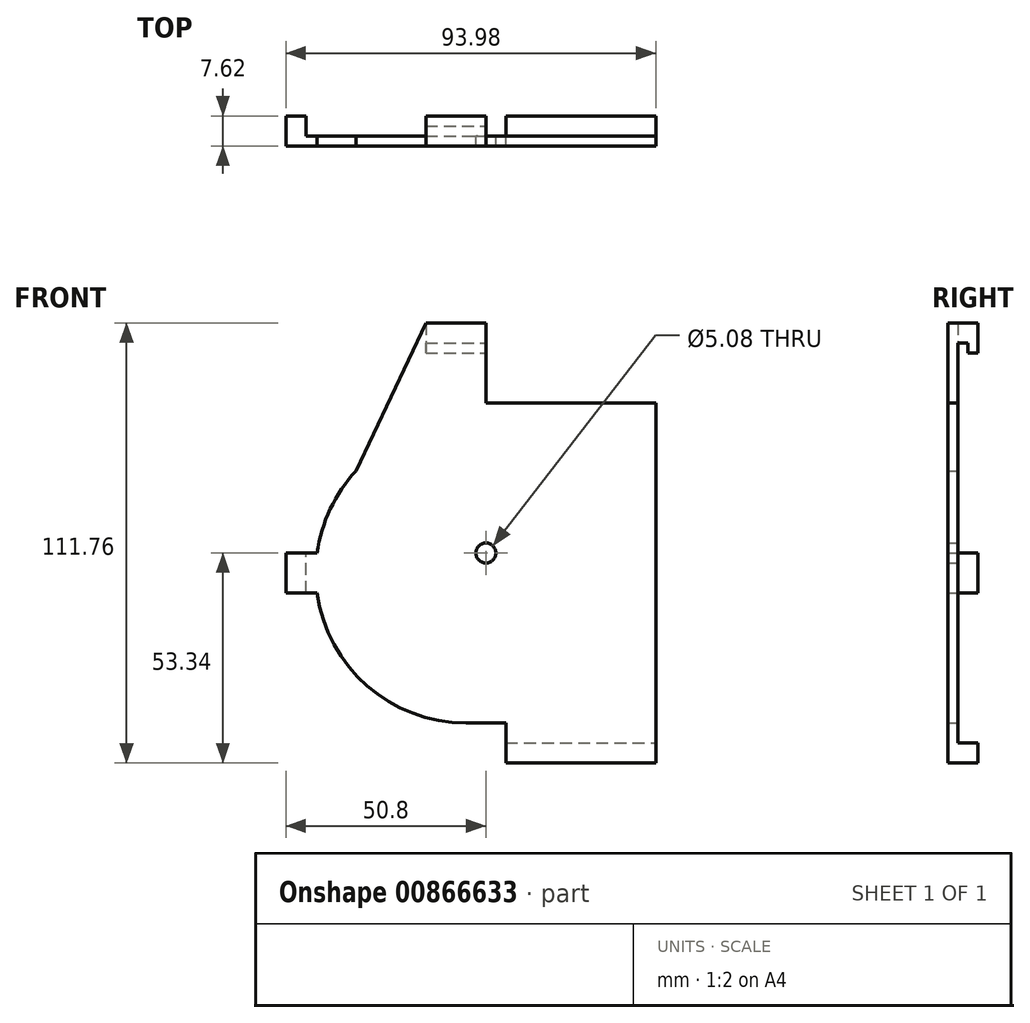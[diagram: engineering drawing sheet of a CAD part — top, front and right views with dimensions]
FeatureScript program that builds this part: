
annotation { "Feature Type Name" : "Feature", "Feature Type Description" : "" }
export const myFeature = defineFeature(function(context is Context, id is Id, definition is map)
    precondition{}
    {
        {
            var Q0;
            Q0=qCreatedBy(makeId("Front.planeOp"),FACE);
            var sketch = newSketch(context, id + "F0", { "sketchPlane" : qUnion([Q0])});
            skLineSegment(sketch, "E0.left", {"start": v(43.18, 43.18) * mm, "end": v(43.18, -38.1) * mm});
            skArc(sketch, "E1", {"start": v(-42.84, -5.08) * mm, "mid": v(-30.16, -28.68) * mm, "end": v(-5.08, -38.1) * mm});
            skLineSegment(sketch, "E2.top", {"start": v(-15.24, 63.5) * mm, "end": v(0, 63.5) * mm});
            skLineSegment(sketch, "E3.top", {"start": v(43.18, 43.18) * mm, "end": v(0, 43.18) * mm});
            skLineSegment(sketch, "E3.right", {"start": v(0, 63.5) * mm, "end": v(0, 43.18) * mm});
            skLineSegment(sketch, "E4.bottom", {"start": v(-50.8, 5.08) * mm, "end": v(-42.84, 5.08) * mm});
            skLineSegment(sketch, "E4.top", {"start": v(-50.8, -5.08) * mm, "end": v(-42.84, -5.08) * mm});
            skLineSegment(sketch, "E4.left", {"start": v(-50.8, 5.08) * mm, "end": v(-50.8, -5.08) * mm});
            skPoint(sketch, "E5.orphan", {"position": v(-43.18, 0) * mm});
            skLineSegment(sketch, "E6", {"start": v(-5.08, -38.1) * mm, "end": v(5.08, -38.1) * mm});
            skLineSegment(sketch, "E7.top", {"start": v(43.18, -48.26) * mm, "end": v(5.08, -48.26) * mm});
            skLineSegment(sketch, "E7.left", {"start": v(43.18, -38.1) * mm, "end": v(43.18, -48.26) * mm});
            skLineSegment(sketch, "E7.right", {"start": v(5.08, -38.1) * mm, "end": v(5.08, -48.26) * mm});
            skArc(sketch, "E8", {"start": v(-32.98, 25.94) * mm, "mid": v(-39.53, 16.28) * mm, "end": v(-42.84, 5.08) * mm});
            skLineSegment(sketch, "E9", {"start": v(0, 63.5) * mm, "end": v(-15.24, 63.5) * mm});
            skLineSegment(sketch, "E10", {"start": v(-32.98, 25.94) * mm, "end": v(-15.24, 63.5) * mm});
            skSolve(sketch);
        }
        {
            var Q0;
            Q0 = qSketchRegion(id + "F0", true);
            extrude(context, id + "F1", {"entities" : qUnion([Q0]), "depth" : 2.54 * mm, "offsetDistance" : 25.4 * mm});
        }
        {
            var Q0;
            Q0=makeQuery(id+"F1.opExtrude","SWEPT_FACE",FACE,{"disambiguationData":[OSD([sQuery(id+"F0.wireOp",EDGE,"E3.right")])]});
            var sketch = newSketch(context, id + "F2", { "sketchPlane" : qUnion([Q0])});
            skLineSegment(sketch, "E11.bottom", {"start": v(0, 63.5) * mm, "end": v(5.08, 63.5) * mm});
            skLineSegment(sketch, "E11.top", {"start": v(2.54, 55.88) * mm, "end": v(5.08, 55.88) * mm});
            skLineSegment(sketch, "E11.left", {"start": v(0, 63.5) * mm, "end": v(0, 58.42) * mm});
            skLineSegment(sketch, "E11.right", {"start": v(5.08, 63.5) * mm, "end": v(5.08, 55.88) * mm});
            skLineSegment(sketch, "E12.top", {"start": v(0, 58.42) * mm, "end": v(2.54, 58.42) * mm});
            skLineSegment(sketch, "E12.right", {"start": v(2.54, 55.88) * mm, "end": v(2.54, 58.42) * mm});
            skSolve(sketch);
        }
        {
            var Q0;
            Q0=makeQuery(id+"F2.imprint","IMPRINT",FACE,{"disambiguationData":[TD([[makeQuery(id+"F2.imprint","IMPRINT",EDGE,{"derivedFrom":sQuery(id+"F2.wireOp",EDGE,"E11.bottom")}),-1.0]])]});
            extrude(context, id + "F3", {"entities" : qUnion([Q0]), "operationType" : NewBodyOperationType.ADD, "oppositeDirection" : true, "depth" : 15.24 * mm, "offsetDistance" : 25.4 * mm});
        }
        {
            var Q0;
            Q0=makeQuery(id+"F1.opExtrude","SWEPT_FACE",FACE,{"disambiguationData":[OSD([sQuery(id+"F0.wireOp",EDGE,"E4.bottom")])]});
            var sketch = newSketch(context, id + "F4", { "sketchPlane" : qUnion([Q0])});
            skLineSegment(sketch, "E13.bottom", {"start": v(-50.8, -2.54) * mm, "end": v(-45.72, -2.54) * mm});
            skLineSegment(sketch, "E13.top", {"start": v(-50.8, 5.08) * mm, "end": v(-45.72, 5.08) * mm});
            skLineSegment(sketch, "E13.left", {"start": v(-50.8, -2.54) * mm, "end": v(-50.8, 5.08) * mm});
            skLineSegment(sketch, "E13.right", {"start": v(-45.72, -2.54) * mm, "end": v(-45.72, 5.08) * mm});
            skSolve(sketch);
        }
        {
            var Q0;
            {var subQ0=sQuery(id+"F4.wireOp",EDGE,"E13.top");Q0=makeQuery(id+"F4.imprint","IMPRINT",FACE,{"disambiguationData":[TD([[makeQuery(id+"F4.imprint","IMPRINT",EDGE,{"derivedFrom":subQ0}),-1.0]])]});}
            extrude(context, id + "F5", {"entities" : qUnion([Q0]), "operationType" : NewBodyOperationType.ADD, "oppositeDirection" : true, "depth" : 10.16 * mm, "offsetDistance" : 25.4 * mm});
        }
        {
            var Q0;
            Q0=makeQuery(id+"F1.opExtrude","CAP_FACE",FACE,{"disambiguationData":[OSD([sQuery(id+"F0.wireOp",EDGE,"E0.top"),sQuery(id+"F0.wireOp",EDGE,"E0.left"),sQuery(id+"F0.wireOp",EDGE,"E1"),sQuery(id+"F0.wireOp",EDGE,"E2.top"),sQuery(id+"F0.wireOp",EDGE,"E3.top"),sQuery(id+"F0.wireOp",EDGE,"E3.right"),sQuery(id+"F0.wireOp",EDGE,"0rXN8d2l-EEdK-oU76-9m5N-EmU7iEtvsEKj"),sQuery(id+"F0.wireOp",EDGE,"cag3bcGU-nAMg-Rm8s-b5UI-sf5c9dMruiX0"),sQuery(id+"F0.wireOp",EDGE,"E4.bottom"),sQuery(id+"F0.wireOp",EDGE,"E4.top"),sQuery(id+"F0.wireOp",EDGE,"E4.left"),sQuery(id+"F0.wireOp",EDGE,"FOCskiKA-atYN-HFuz-2flS-ZA1Z71375tWF.top"),sQuery(id+"F0.wireOp",EDGE,"FOCskiKA-atYN-HFuz-2flS-ZA1Z71375tWF.left"),sQuery(id+"F0.wireOp",EDGE,"FOCskiKA-atYN-HFuz-2flS-ZA1Z71375tWF.right")])],"isStart":true});
            var sketch = newSketch(context, id + "F6", { "sketchPlane" : qUnion([Q0])});
            skCircle(sketch, "E14", {"center": v(0, 5.08) * mm, "radius": 2.54 * mm});
            skSolve(sketch);
        }
        {
            var Q0;
            Q0=makeQuery(id+"F6.imprint","IMPRINT",FACE,{"disambiguationData":[TD([[makeQuery(id+"F6.imprint","IMPRINT",EDGE,{"derivedFrom":sQuery(id+"F6.wireOp",EDGE,"E14")}),1.0]])]});
            var Q1;
            Q1=sQuery(id+"F6.wireOp",EDGE,"E14");
            extrude(context, id + "F7", {"entities" : qUnion([Q0]), "operationType" : NewBodyOperationType.REMOVE, "surfaceEntities" : qUnion([Q1]), "oppositeDirection" : true, "depth" : 25.4 * mm, "offsetDistance" : 25.4 * mm});
        }
        {
            var Q0;
            Q0=makeQuery(id+"F1.opExtrude","SWEPT_FACE",FACE,{"disambiguationData":[OSD([sQuery(id+"F0.wireOp",EDGE,"E0.left"),sQuery(id+"F0.wireOp",EDGE,"E7.left")])]});
            var sketch = newSketch(context, id + "F8", { "sketchPlane" : qUnion([Q0])});
            skLineSegment(sketch, "E15.bottom", {"start": v(-2.54, -48.26) * mm, "end": v(5.08, -48.26) * mm});
            skLineSegment(sketch, "E15.top", {"start": v(-2.54, -43.18) * mm, "end": v(5.08, -43.18) * mm});
            skLineSegment(sketch, "E15.left", {"start": v(-2.54, -48.26) * mm, "end": v(-2.54, -43.18) * mm});
            skLineSegment(sketch, "E15.right", {"start": v(5.08, -48.26) * mm, "end": v(5.08, -43.18) * mm});
            skSolve(sketch);
        }
        {
            var Q0;
            {var subQ5=sQuery(id+"F8.wireOp",EDGE,"E15.left");Q0=makeQuery(id+"F8.imprint","IMPRINT",FACE,{"disambiguationData":[TD([[makeQuery(id+"F8.imprint","IMPRINT",EDGE,{"derivedFrom":subQ5}),1.0]])]});}
            var Q1;
            {var subQ3=sQuery(id+"F8.wireOp",EDGE,"E15.right");Q1=makeQuery(id+"F8.imprint","IMPRINT",FACE,{"disambiguationData":[TD([[makeQuery(id+"F8.imprint","IMPRINT",EDGE,{"derivedFrom":subQ3}),1.0]])]});}
            extrude(context, id + "F9", {"entities" : qUnion([Q0, Q1]), "operationType" : NewBodyOperationType.ADD, "oppositeDirection" : true, "depth" : 38.1 * mm, "offsetDistance" : 25.4 * mm});
        }
    });
